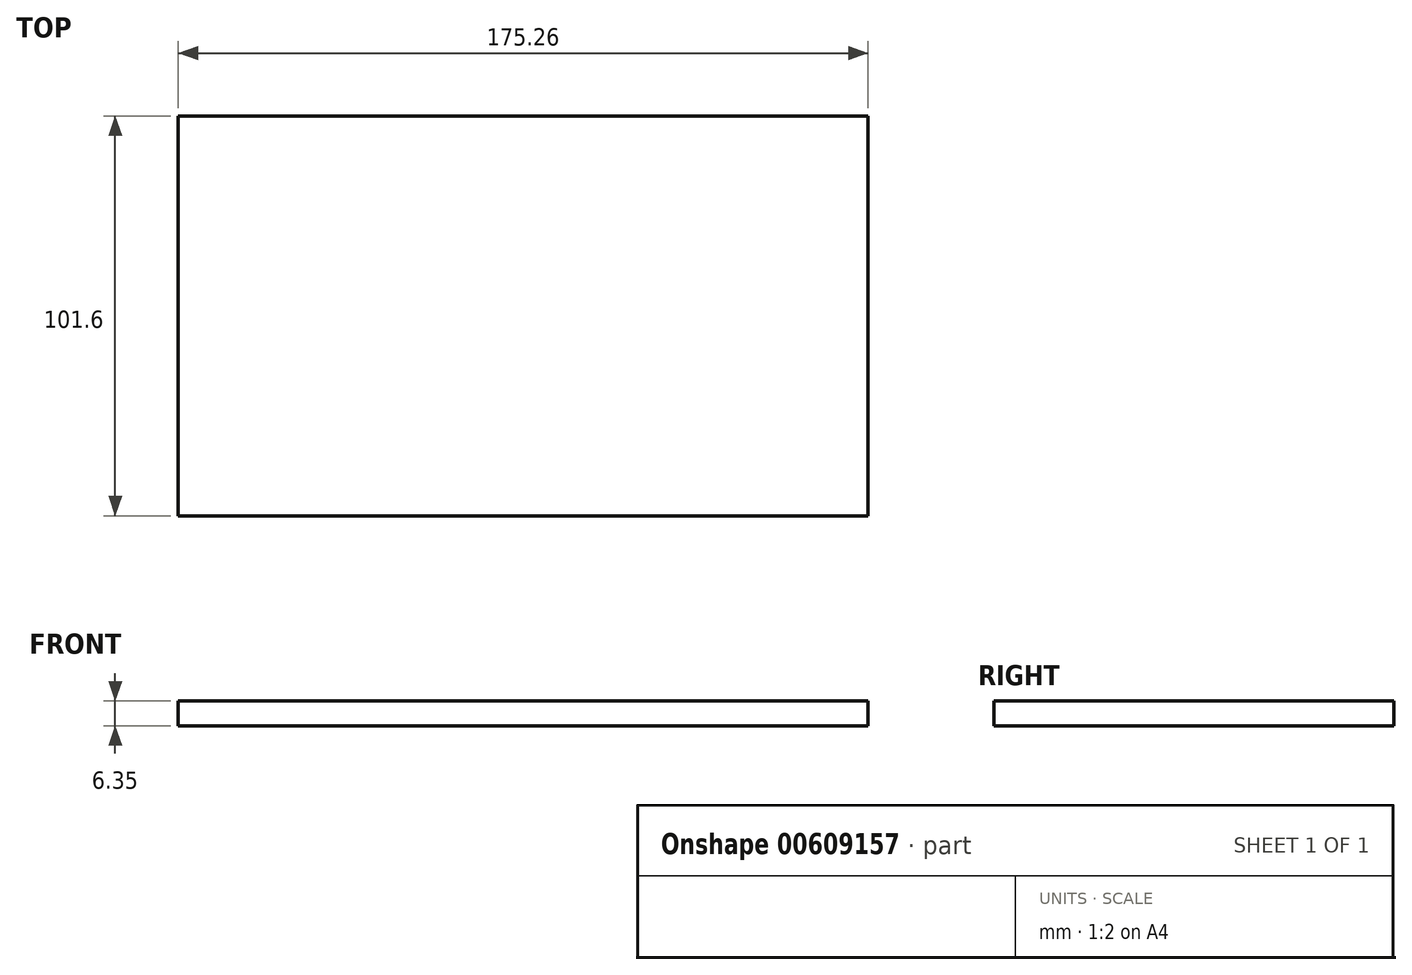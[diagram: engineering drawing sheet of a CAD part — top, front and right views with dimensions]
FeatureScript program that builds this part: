
annotation { "Feature Type Name" : "Feature", "Feature Type Description" : "" }
export const myFeature = defineFeature(function(context is Context, id is Id, definition is map)
    precondition{}
    {
        {
            var Q0;
            Q0=qCreatedBy(makeId("Top.planeOp"),FACE);
            var sketch = newSketch(context, id + "F0", { "sketchPlane" : qUnion([Q0])});
            skLineSegment(sketch, "E0.bottom", {"start": v(0, 0) * mm, "end": v(175.26, 0) * mm});
            skLineSegment(sketch, "E0.top", {"start": v(0, 101.6) * mm, "end": v(175.26, 101.6) * mm});
            skLineSegment(sketch, "E0.left", {"start": v(0, 0) * mm, "end": v(0, 101.6) * mm});
            skLineSegment(sketch, "E0.right", {"start": v(175.26, 0) * mm, "end": v(175.26, 101.6) * mm});
            skSolve(sketch);
        }
        {
            var Q0;
            Q0=makeQuery(id+"F0.imprint","IMPRINT",FACE,{"disambiguationData":[TD([[makeQuery(id+"F0.imprint","IMPRINT",EDGE,{"derivedFrom":sQuery(id+"F0.wireOp",EDGE,"E0.bottom")}),1.0]])]});
            extrude(context, id + "F1", {"entities" : qUnion([Q0]), "depth" : 6.35 * mm, "offsetDistance" : 25.4 * mm});
        }
    });
